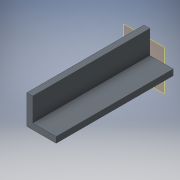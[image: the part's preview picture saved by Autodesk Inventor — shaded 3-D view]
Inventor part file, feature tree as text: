
AUTODESK INVENTOR PART (.ipt)
format: ipt  version: 2016 (Build 200138000, 138)  size: 134,656 bytes
history: native  units: in
note: dims shown in document units (in); Inventor stores cm internally (conversion verified against a paired STEP export)
features: other x21, plane x1, extrude x1, sketch x1
ambient origin geometry x8: Origin, YZ Plane, XZ Plane, XY Plane, X Axis, Y Axis, Z Axis, Center Point
bodies: Body1 (feature_tree)
feature tree (24):
  other  "A_19"
  other  "A_20"
  other  "A_21"
  other  "A_22"
  other  "A_23"
  other  "A_24"
  other  "A_25"
  other  "A_26"
  other  "A_27"
  other  "A_28"
  other  "A_29"
  other  "A_30"
  other  "A_31"
  other  "A_32"
  other  "A_33"
  other  "A_34"
  other  "A_35"
  other  "A_36"
  other  "FRONT"
  other  "TOP"
  other  "RIGHT"
  plane  "Work Plane4"
  extrude  "Extrusion1"  [1 undecoded]
  sketch  "Sketch1"  dims[d0=2.5197in d1=0.0in]
note: 1 required parameter value undecoded (feature->parameter linkage not recoverable at this tier; creation-order binding heuristic only, values carry confidence <= 0.55)
